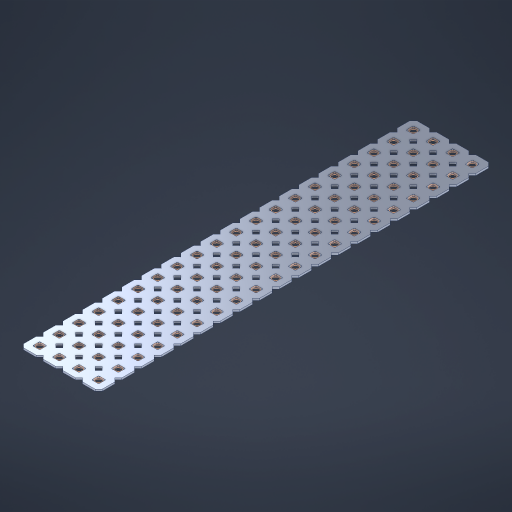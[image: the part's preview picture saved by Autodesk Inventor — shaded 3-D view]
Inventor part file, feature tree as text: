
AUTODESK INVENTOR PART (.ipt)
format: ipt  version: 2023 (Build 270158000, 158)  size: 1,183,232 bytes
history: native  units: in
note: dims shown in document units (in); Inventor stores cm internally (conversion verified against a paired STEP export)
features: other x81, extrude x79, sketch x2, pattern_linear x1
ambient origin geometry x8: Origin, YZ Plane, XZ Plane, XY Plane, X Axis, Y Axis, Z Axis, Center Point
bodies: Solid1 (feature_tree), Body (feature_tree)
feature tree (163):
  pattern_linear  "Rectangular Pattern1"  Spacing1=0.09in  [1 undecoded]
  sketch  "Sketch1"  dims[d1=0.5in]
  sketch  "Sketch2"  dims[d2=0.182in d3=0.09in d4=0.09in d5=0.09in d6=0.09in d7=0.09in d8=0.09in d9=0.09in d10=0.09in d11=0.02in d13=0.0in d14=0.172in d15=0.0625in d16=0.0in d19=0.5in d22=0.5in]
  other  "Srf1"
  other  "Srf126"
  other  "Srf127"
  other  "Srf128"
  other  "Srf129"
  other  "Srf130"
  other  "Srf131"
  other  "Srf250"
  other  "Srf251"
  other  "Srf252"
  other  "Srf253"
  other  "Srf254"
  other  "Srf255"
  other  "Srf256"
  other  "Srf257"
  other  "Srf258"
  other  "Srf259"
  other  "Srf260"
  other  "Srf261"
  other  "Srf262"
  other  "Srf268"
  other  "Srf269"
  other  "Srf270"
  other  "Srf271"
  other  "Srf272"
  other  "Srf273"
  other  "Srf274"
  other  "Srf275"
  other  "Srf276"
  other  "Srf277"
  other  "Srf278"
  other  "Srf279"
  other  "Srf280"
  other  "Srf281"
  other  "Srf282"
  other  "Srf283"
  other  "Srf284"
  other  "Srf285"
  other  "Srf286"
  other  "Srf287"
  other  "Srf293"
  other  "Srf294"
  other  "Srf295"
  other  "Srf296"
  other  "Srf297"
  other  "Srf298"
  other  "Srf299"
  other  "Srf300"
  other  "Srf301"
  other  "Srf302"
  other  "Srf303"
  other  "Srf304"
  other  "Srf305"
  other  "Srf306"
  other  "Srf307"
  other  "Srf308"
  other  "Srf309"
  other  "Srf310"
  other  "Srf311"
  other  "Srf312"
  other  "Srf318"
  other  "Srf319"
  other  "Srf320"
  other  "Srf321"
  other  "Srf322"
  other  "Srf323"
  other  "Srf324"
  other  "Srf325"
  other  "Srf326"
  other  "Srf327"
  other  "Srf328"
  other  "Srf329"
  other  "Srf330"
  other  "Srf331"
  other  "Srf332"
  other  "Srf333"
  other  "Srf334"
  other  "Srf335"
  other  "Srf336"
  other  "Srf337"
  other  "Circle"
  extrude  "ExtrusionSrf126"  Depth=0.09in
  extrude  "ExtrusionSrf127"  Depth=0.09in
  extrude  "ExtrusionSrf128"  Depth=0.09in
  extrude  "ExtrusionSrf129"  Depth=0.09in
  extrude  "ExtrusionSrf130"  Depth=0.09in
  extrude  "ExtrusionSrf131"  Depth=0.09in
  extrude  "ExtrusionSrf250"  Depth=0.09in
  extrude  "ExtrusionSrf251"  Depth=0.02in
  extrude  "ExtrusionSrf252"  TaperAngle=0.0deg  [1 undecoded]
  extrude  "ExtrusionSrf253"  Depth=0.5in
  extrude  "ExtrusionSrf254"  Depth=0.5in TaperAngle=0.0deg
  extrude  "ExtrusionSrf255"  Depth=0.5in
  extrude  "ExtrusionSrf256"  Depth=0.5in
  extrude  "ExtrusionSrf257"  [1 undecoded]
  extrude  "ExtrusionSrf258"  [1 undecoded]
  extrude  "ExtrusionSrf259"  [1 undecoded]
  extrude  "ExtrusionSrf260"  [1 undecoded]
  extrude  "ExtrusionSrf261"  [1 undecoded]
  extrude  "ExtrusionSrf262"  [1 undecoded]
  extrude  "ExtrusionSrf268"  [1 undecoded]
  extrude  "ExtrusionSrf269"  [1 undecoded]
  extrude  "ExtrusionSrf270"  [1 undecoded]
  extrude  "ExtrusionSrf271"  [1 undecoded]
  extrude  "ExtrusionSrf272"  [1 undecoded]
  extrude  "ExtrusionSrf273"  [1 undecoded]
  extrude  "ExtrusionSrf274"  [1 undecoded]
  extrude  "ExtrusionSrf275"  [1 undecoded]
  extrude  "ExtrusionSrf276"  [1 undecoded]
  extrude  "ExtrusionSrf277"  [1 undecoded]
  extrude  "ExtrusionSrf278"  [1 undecoded]
  extrude  "ExtrusionSrf279"  [1 undecoded]
  extrude  "ExtrusionSrf280"  [1 undecoded]
  extrude  "ExtrusionSrf281"  [1 undecoded]
  extrude  "ExtrusionSrf282"  [1 undecoded]
  extrude  "ExtrusionSrf283"  [1 undecoded]
  extrude  "ExtrusionSrf284"  [1 undecoded]
  extrude  "ExtrusionSrf285"  [1 undecoded]
  extrude  "ExtrusionSrf286"  [1 undecoded]
  extrude  "ExtrusionSrf287"  [1 undecoded]
  extrude  "ExtrusionSrf293"  [1 undecoded]
  extrude  "ExtrusionSrf294"  [1 undecoded]
  extrude  "ExtrusionSrf295"  [1 undecoded]
  extrude  "ExtrusionSrf296"  [1 undecoded]
  extrude  "ExtrusionSrf297"  [1 undecoded]
  extrude  "ExtrusionSrf298"  [1 undecoded]
  extrude  "ExtrusionSrf299"  [1 undecoded]
  extrude  "ExtrusionSrf300"  [1 undecoded]
  extrude  "ExtrusionSrf301"  [1 undecoded]
  extrude  "ExtrusionSrf302"  [1 undecoded]
  extrude  "ExtrusionSrf303"  [1 undecoded]
  extrude  "ExtrusionSrf304"  [1 undecoded]
  extrude  "ExtrusionSrf305"  [1 undecoded]
  extrude  "ExtrusionSrf306"  [1 undecoded]
  extrude  "ExtrusionSrf307"  [1 undecoded]
  extrude  "ExtrusionSrf308"  [1 undecoded]
  extrude  "ExtrusionSrf309"  [1 undecoded]
  extrude  "ExtrusionSrf310"  [1 undecoded]
  extrude  "ExtrusionSrf311"  [1 undecoded]
  extrude  "ExtrusionSrf312"  [1 undecoded]
  extrude  "ExtrusionSrf318"  [1 undecoded]
  extrude  "ExtrusionSrf319"  [1 undecoded]
  extrude  "ExtrusionSrf320"  [1 undecoded]
  extrude  "ExtrusionSrf321"  [1 undecoded]
  extrude  "ExtrusionSrf322"  [1 undecoded]
  extrude  "ExtrusionSrf323"  [1 undecoded]
  extrude  "ExtrusionSrf324"  [1 undecoded]
  extrude  "ExtrusionSrf325"  [1 undecoded]
  extrude  "ExtrusionSrf326"  [1 undecoded]
  extrude  "ExtrusionSrf327"  [1 undecoded]
  extrude  "ExtrusionSrf328"  [1 undecoded]
  extrude  "ExtrusionSrf329"  [1 undecoded]
  extrude  "ExtrusionSrf330"  [1 undecoded]
  extrude  "ExtrusionSrf331"  [1 undecoded]
  extrude  "ExtrusionSrf332"  [1 undecoded]
  extrude  "ExtrusionSrf333"  [1 undecoded]
  extrude  "ExtrusionSrf334"  [1 undecoded]
  extrude  "ExtrusionSrf335"  [1 undecoded]
  extrude  "ExtrusionSrf336"  [1 undecoded]
  extrude  "ExtrusionSrf337"  [1 undecoded]
note: 68 required parameter values undecoded (feature->parameter linkage not recoverable at this tier; creation-order binding heuristic only, values carry confidence <= 0.55)
